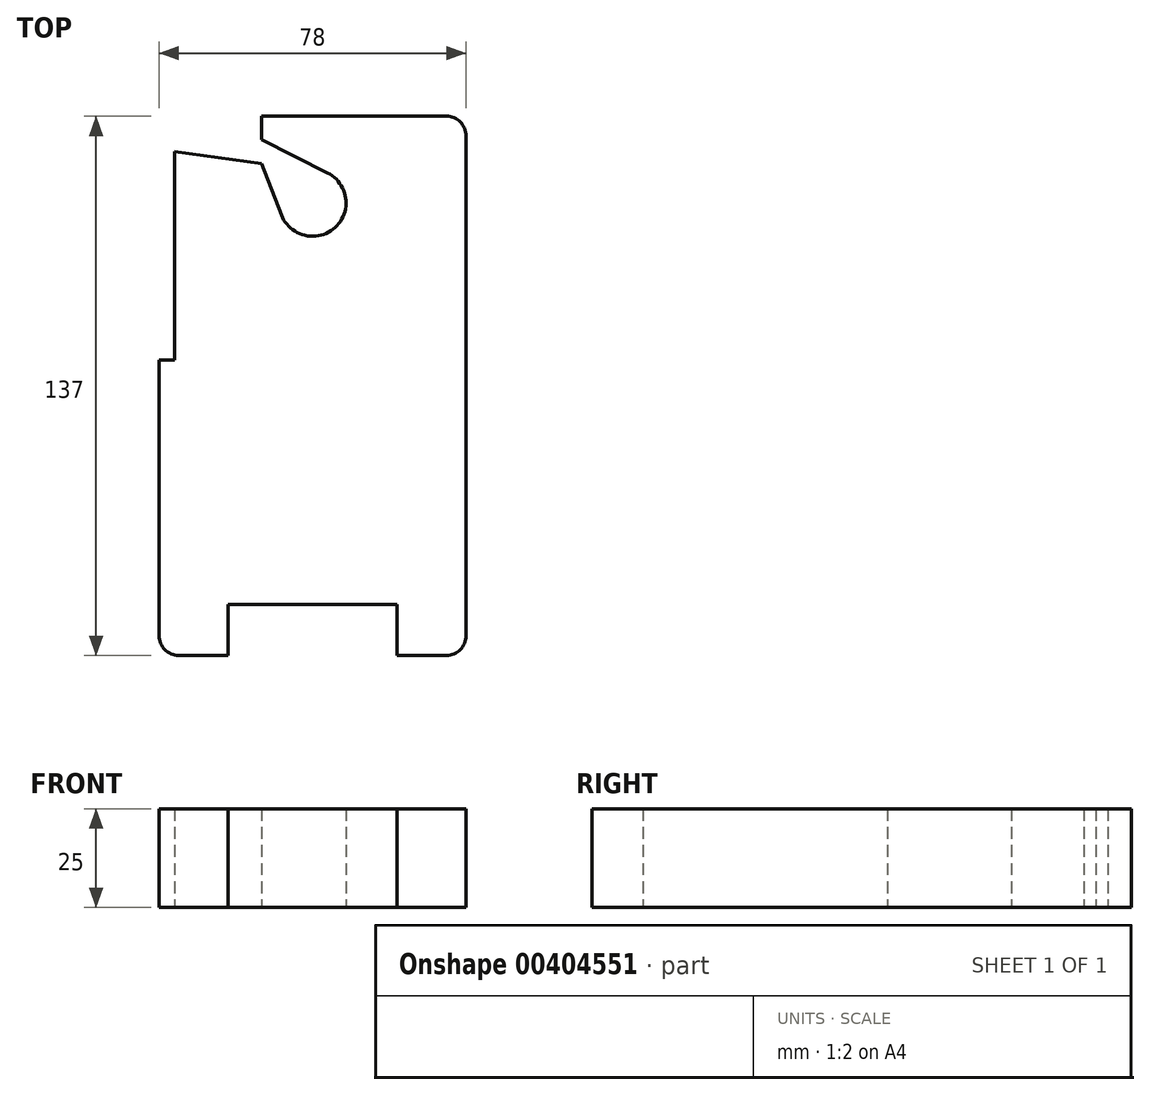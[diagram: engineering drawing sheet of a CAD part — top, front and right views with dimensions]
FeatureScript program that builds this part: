
annotation { "Feature Type Name" : "Feature", "Feature Type Description" : "" }
export const myFeature = defineFeature(function(context is Context, id is Id, definition is map)
    precondition{}
    {
        {
            var Q0;
            Q0=qCreatedBy(makeId("Top.planeOp"),FACE);
            var sketch = newSketch(context, id + "F0", { "sketchPlane" : qUnion([Q0])});
            skLineSegment(sketch, "E0.bottom", {"start": v(35, -68.5) * mm, "end": v(-30, -68.5) * mm});
            skLineSegment(sketch, "E0.top", {"start": v(35, 68.5) * mm, "end": v(-35, 68.5) * mm});
            skLineSegment(sketch, "E0.right", {"start": v(-35, -45.64) * mm, "end": v(-35, 68.5) * mm});
            skPoint(sketch, "E0.middle", {"position": v(0, 0) * mm});
            skLineSegment(sketch, "E1.bottom", {"start": v(21.5, -55.5) * mm, "end": v(-21.5, -55.5) * mm});
            skLineSegment(sketch, "E1.left", {"start": v(21.5, -55.5) * mm, "end": v(21.5, -68.5) * mm});
            skLineSegment(sketch, "E1.right", {"start": v(-21.5, -55.5) * mm, "end": v(-21.5, -68.5) * mm});
            skPoint(sketch, "E1.middle", {"position": v(0, -68.5) * mm});
            skPoint(sketch, "E2.start.orphan", {"position": v(0, -55.5) * mm});
            skLineSegment(sketch, "E3.bottom", {"start": v(34, -68.5) * mm, "end": v(35, -68.5) * mm});
            skLineSegment(sketch, "E3.top", {"start": v(34, 68.5) * mm, "end": v(35, 68.5) * mm});
            skLineSegment(sketch, "E3.right", {"start": v(39, -63.5) * mm, "end": v(39, 63.5) * mm});
            skLineSegment(sketch, "E4.bottom", {"start": v(-30, 68.5) * mm, "end": v(-13, 68.5) * mm});
            skLineSegment(sketch, "E4.top", {"start": v(-35, 56.5) * mm, "end": v(-13, 56.5) * mm});
            skLineSegment(sketch, "E4.left", {"start": v(-35, 59.5) * mm, "end": v(-35, 56.5) * mm});
            skLineSegment(sketch, "E4.right", {"start": v(-13, 68.5) * mm, "end": v(-13, 56.5) * mm});
            skCircle(sketch, "E5", {"center": v(0, 46.5) * mm, "radius": 8.5 * mm});
            skLineSegment(sketch, "E6", {"start": v(0, 46.5) * mm, "end": v(0, 68.5) * mm});
            skLineSegment(sketch, "E7", {"start": v(-13, 62.5) * mm, "end": v(3.8, 54.1) * mm});
            skLineSegment(sketch, "E8", {"start": v(-13, 56.5) * mm, "end": v(-7.92, 43.42) * mm});
            skLineSegment(sketch, "E9.bottom", {"start": v(-34, -68.5) * mm, "end": v(-35, -68.5) * mm});
            skLineSegment(sketch, "E9.top", {"start": v(-35, 6.5) * mm, "end": v(-39, 6.5) * mm});
            skLineSegment(sketch, "E9.left", {"start": v(-35, -68.5) * mm, "end": v(-35, 6.5) * mm});
            skLineSegment(sketch, "E9.right", {"start": v(-39, -63.5) * mm, "end": v(-39, 6.5) * mm});
            skPoint(sketch, "E10.visualSharp", {"position": v(-35, 68.5) * mm});
            skPoint(sketch, "E11.visualSharp", {"position": v(-35, -68.5) * mm});
            skPoint(sketch, "E12.visualSharp", {"position": v(39, -68.5) * mm});
            skArc(sketch, "E12.filletArc", {"start": v(34, -68.5) * mm, "mid": v(37.54, -67.04) * mm, "end": v(39, -63.5) * mm});
            skPoint(sketch, "E13.visualSharp", {"position": v(39, 68.5) * mm});
            skArc(sketch, "E13.filletArc", {"start": v(39, 63.5) * mm, "mid": v(37.54, 67.04) * mm, "end": v(34, 68.5) * mm});
            skPoint(sketch, "E14.visualSharp", {"position": v(-39, -68.5) * mm});
            skArc(sketch, "E14.filletArc", {"start": v(-39, -63.5) * mm, "mid": v(-37.54, -67.04) * mm, "end": v(-34, -68.5) * mm});
            skLineSegment(sketch, "E15", {"start": v(-30, -68.5) * mm, "end": v(-34, -68.5) * mm});
            skLineSegment(sketch, "E16", {"start": v(-35, 59.5) * mm, "end": v(-13, 56.5) * mm});
            skSolve(sketch);
        }
        {
            var Q0;
            Q0=makeQuery(id+"F0.imprint","IMPRINT",FACE,{"disambiguationData":[TD([[makeQuery(id+"F0.imprint","IMPRINT",EDGE,{"derivedFrom":sQuery(id+"F0.wireOp",EDGE,"E1.bottom")}),-1.0]])]});
            var Q1;
            {var subQ2=sQuery(id+"F0.wireOp",EDGE,"E9.top");Q1=makeQuery(id+"F0.imprint","IMPRINT",FACE,{"disambiguationData":[TD([[makeQuery(id+"F0.imprint","IMPRINT",EDGE,{"derivedFrom":subQ2}),1.0]])]});}
            var Q2;
            {var subQ1=sQuery(id+"F0.wireOp",EDGE,"E0.top");var subQ3=sQuery(id+"F0.wireOp",EDGE,"E6");var subQ4=makeQuery(id+"F0.imprint","INTERSECT",VERTEX,{"derivedFrom":[subQ1,subQ3]});Q2=makeQuery(id+"F0.imprint","IMPRINT",FACE,{"disambiguationData":[TD([[makeQuery(id+"F0.imprint","IMPRINT",EDGE,{"disambiguationData":[TD([[subQ4,1.0]])],"derivedFrom":subQ3}),1.0]])]});}
            var Q3;
            Q3=makeQuery(id+"F0.imprint","IMPRINT",FACE,{"disambiguationData":[TD([[makeQuery(id+"F0.imprint","IMPRINT",EDGE,{"derivedFrom":sQuery(id+"F0.wireOp",EDGE,"E4.top")}),1.0]])]});
            extrude(context, id + "F1", {"entities" : qUnion([Q0, Q1, Q2, Q3]), "depth" : 25 * mm});
        }
    });
